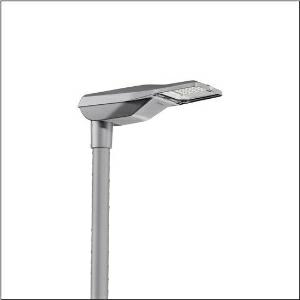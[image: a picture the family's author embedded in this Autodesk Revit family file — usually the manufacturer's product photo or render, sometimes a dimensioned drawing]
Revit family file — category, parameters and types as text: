
# Revit family: streetlight_sl_21_iq_micro___p0_8a_5xe1u31d08cb_216c
name_source: partatom
category: Lighting Fixtures
units: mm (PartAtom-declared; Revit-internal decimal feet)

## family parameters
Cut with Voids When Loaded = No
Host = Face
Light Source = No
Part Type = Normal
Room Calculation Point = No
Round Connector Dimension = Use Diameter
Shared = No

## types (1)
- --- (1 x LED, 2830 lm, 19.4 W, 3000K)
    Apparent Load = 19 VA
    CIE Flux Codes = 33 69 96 100 100
    Color Rendering = 70
    Color Temperature = 3000K
    Default Elevation = 1800 mm
    Description = Streetlight SL 21 iQ micro, mast luminaire, primary light control with lens, of PMMA, primary optical cover: cover, of toughened safety glass, transparent, light distribution: P0.8a, light emission: direct distribution, primary light characteristic: asymmetric, installation type: post-top, side-entry, LED, High Power LED, rated luminous flux: 2.830lm, luminous efficacy: 146lm/W, light colour: 730, colour temperature: 3000K, control gear: iQ-Comfort, control: pre-setting: linear dimming characteristic, Auto-Match, Temp-Guard, Lumen-Switch, Night-Set, Smart-Wire, Light-Fading, Desk-Remote (wireless, voltage-free reading and setting of iQ features in the workshop via application-optimized NFC function/RFID function), optimised constant luminous flux control (CLO 2.0), mains connection: 220..240V, AC, 50/60Hz, start of lifetime: 19W, end of service life: 20W, reduction: 10W, luminaire housing, of diecast aluminium, powder-coated, SITECO metallic grey (DB 702S), corrosivity category C5 high according to DIN EN ISO 12944, please order mast flange separately, inclination adjustable: 0°, 5°, 10°, 15°, sealing non-destructively replaceable, multi-level sealing system, length: 528mm, width: 235mm, height: 110mm, mast flange for spigot size: 42mm (side-entry): 5XC10008XM4, 60/48mm (side-entry/post-top): 5XC10108XM2, 76/60mm (side-entry/post-top): 5XC10108XM1, protection rating (complete): IP66, insulation class (complete): insulation class II (safety insulation), certification: CE, ENEC, ENEC+, VDE, impact resistance: IK10, permissible operating ambient temperature for outdoor applications: -40..+50°C, standard-compliant lighting for roads and squares, packaging unit: 1 piece

Light Distribution: P0.8a
    Height = 110 mm
    Lamp = 1 x LED
    Lamp Light Flux = 2830 lm
    Lamp Power = 19.4 W
    Lamp count = 1
    Length = 528 mm
    Luminous efficacy = 146 lm/W
    Manufacturer = Siteco
    ModVariant = No
    Model = 5XE1U31D08CB
    Number of Poles = 1
    OnlyDefault = Yes
    Power Factor = 1
    Product Name = Streetlight SL 21 iQ micro | P0.8a
    Product group = mast luminaire | pylon top
    ProductGroupID = 6100
    Protection Class = Protection class II
    Protection Degree = IP 66
    RLX_Detail_Level = 1
    RLX_Emergency_Light_Flux = 0 lm
    RLX_Emergency_Type = 0
    RLX_Emergency_Type_DB = No
    RlxData = <blob elided: 99409 chars, md5=73f14d6f>
    Socket = socket
    Standby Power = 0 W
    System Light Flux = 2830 lm
    System Power = 19 W
    Type Comments = factory setting: luminous flux: 100 % | dim-lin: 254 | 387 mA
    Type Image = l_1006881.jpg
    URL = http://relux.com
    VarID = @adj_080781
    Voltage = 0 V
    Weight = 0.00 kg
    Width = 235 mm

## geometry (parser evidence)
native form markers: Blend x4, Sweep x9
no freeform markers — native parametric forms only
